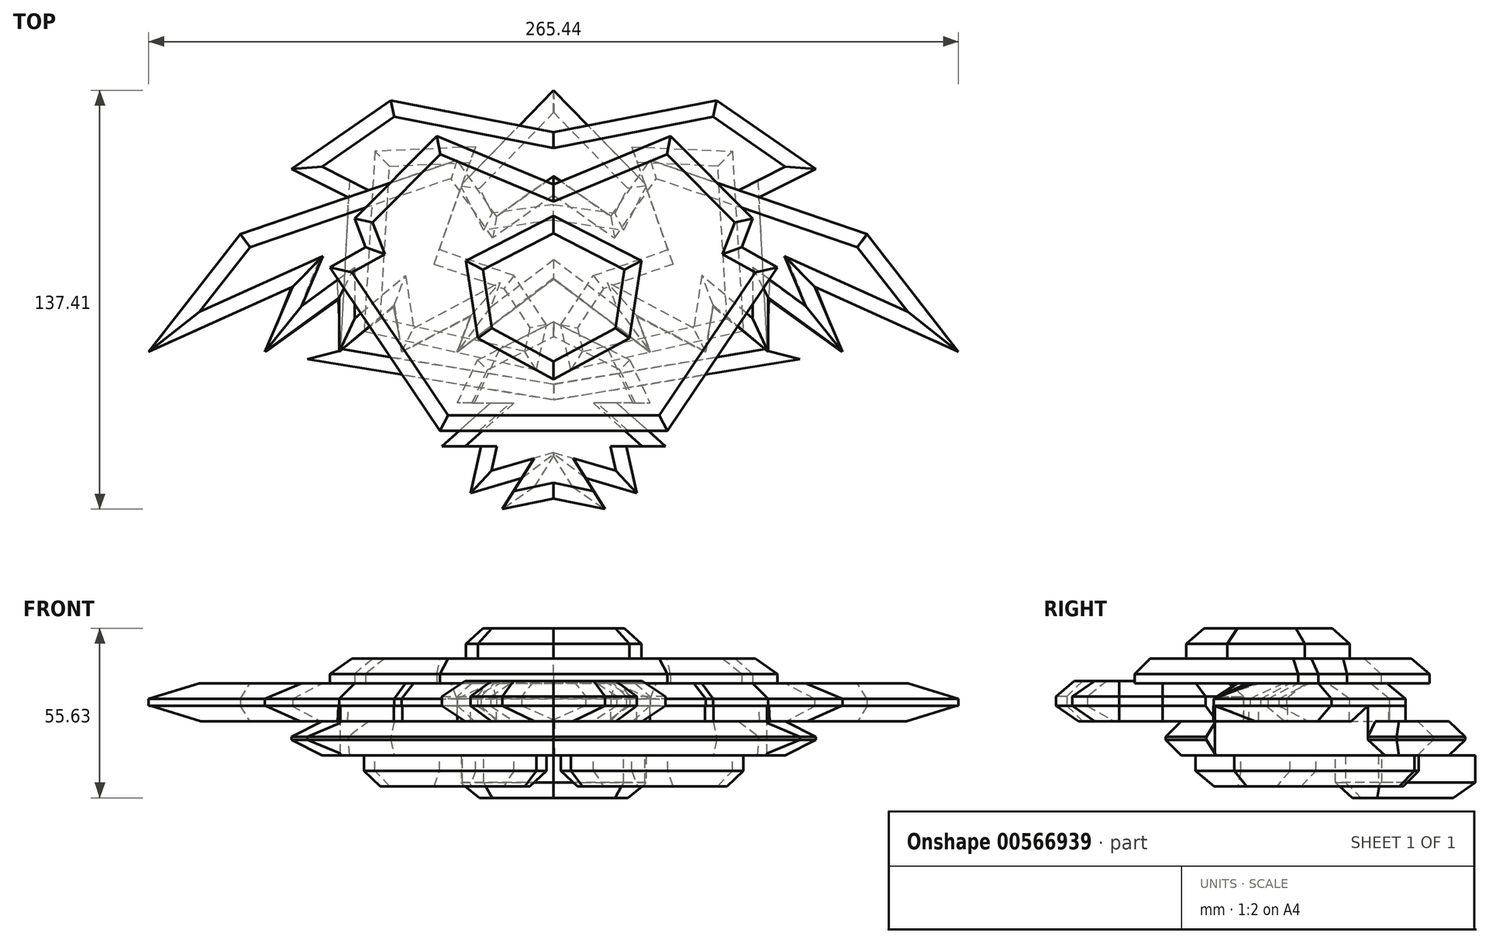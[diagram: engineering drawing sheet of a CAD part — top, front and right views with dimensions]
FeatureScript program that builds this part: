
annotation { "Feature Type Name" : "Feature", "Feature Type Description" : "" }
export const myFeature = defineFeature(function(context is Context, id is Id, definition is map)
    precondition{}
    {
        {
            var Q0;
            Q0=qCreatedBy(makeId("Top.planeOp"),FACE);
            var sketch = newSketch(context, id + "F0", { "sketchPlane" : qUnion([Q0])});
            skLineSegment(sketch, "E0", {"start": v(0, 55.5) * mm, "end": v(-18.73, 42.35) * mm});
            skLineSegment(sketch, "E1", {"start": v(-18.73, 42.35) * mm, "end": v(-31.67, 60.77) * mm});
            skLineSegment(sketch, "E2", {"start": v(-31.67, 60.77) * mm, "end": v(-102.63, 36.57) * mm});
            skLineSegment(sketch, "E3", {"start": v(-102.63, 36.57) * mm, "end": v(-132.72, -2.1) * mm});
            skLineSegment(sketch, "E4", {"start": v(-132.72, -2.1) * mm, "end": v(-85.5, 19.23) * mm});
            skLineSegment(sketch, "E5", {"start": v(-85.5, 19.23) * mm, "end": v(-94.66, -2.1) * mm});
            skLineSegment(sketch, "E6", {"start": v(-94.66, -2.1) * mm, "end": v(-70.35, 15.64) * mm});
            skLineSegment(sketch, "E7", {"start": v(-70.35, 15.64) * mm, "end": v(-70.35, -2.1) * mm});
            skLineSegment(sketch, "E8", {"start": v(-70.35, -2.1) * mm, "end": v(-52.21, 13.25) * mm});
            skLineSegment(sketch, "E9", {"start": v(-52.21, 13.25) * mm, "end": v(-49.82, -2.1) * mm});
            skLineSegment(sketch, "E10", {"start": v(-49.82, -2.1) * mm, "end": v(-27.1, 9.86) * mm});
            skLineSegment(sketch, "E11", {"start": v(-27.1, 9.86) * mm, "end": v(-31.67, -2.1) * mm});
            skLineSegment(sketch, "E12", {"start": v(-31.67, -2.1) * mm, "end": v(0, 21.82) * mm});
            skLineSegment(sketch, "E13", {"start": v(0, 21.82) * mm, "end": v(0, 55.5) * mm});
            skSolve(sketch);
        }
        {
            var Q0;
            Q0=makeQuery(id+"F0.imprint","IMPRINT",FACE,{"disambiguationData":[TD([[makeQuery(id+"F0.imprint","IMPRINT",EDGE,{"derivedFrom":sQuery(id+"F0.wireOp",EDGE,"E0")}),1.0]])]});
            extrude(context, id + "F1", {"entities" : qUnion([Q0]), "depth" : 7.37 * mm, "offsetDistance" : 25.4 * mm});
        }
        {
            var Q0;
            Q0=makeQuery(id+"F1.opExtrude","CAP_EDGE",EDGE,{"disambiguationData":[OSD([sQuery(id+"F0.wireOp",EDGE,"E2")])],"isStart":false});
            var Q1;
            Q1=makeQuery(id+"F1.opExtrude","CAP_EDGE",EDGE,{"disambiguationData":[OSD([sQuery(id+"F0.wireOp",EDGE,"E1")])],"isStart":false});
            var Q2;
            Q2=makeQuery(id+"F1.opExtrude","CAP_EDGE",EDGE,{"disambiguationData":[OSD([sQuery(id+"F0.wireOp",EDGE,"E0")])],"isStart":false});
            var Q3;
            Q3=makeQuery(id+"F1.opExtrude","CAP_EDGE",EDGE,{"disambiguationData":[OSD([sQuery(id+"F0.wireOp",EDGE,"E3")])],"isStart":false});
            var Q4;
            Q4=makeQuery(id+"F1.opExtrude","CAP_EDGE",EDGE,{"disambiguationData":[OSD([sQuery(id+"F0.wireOp",EDGE,"E4")])],"isStart":false});
            var Q5;
            Q5=makeQuery(id+"F1.opExtrude","CAP_EDGE",EDGE,{"disambiguationData":[OSD([sQuery(id+"F0.wireOp",EDGE,"E5")])],"isStart":false});
            var Q6;
            Q6=makeQuery(id+"F1.opExtrude","CAP_EDGE",EDGE,{"disambiguationData":[OSD([sQuery(id+"F0.wireOp",EDGE,"E6")])],"isStart":false});
            var Q7;
            Q7=makeQuery(id+"F1.opExtrude","CAP_EDGE",EDGE,{"disambiguationData":[OSD([sQuery(id+"F0.wireOp",EDGE,"E7")])],"isStart":false});
            var Q8;
            Q8=makeQuery(id+"F1.opExtrude","CAP_EDGE",EDGE,{"disambiguationData":[OSD([sQuery(id+"F0.wireOp",EDGE,"E8")])],"isStart":false});
            var Q9;
            Q9=makeQuery(id+"F1.opExtrude","CAP_EDGE",EDGE,{"disambiguationData":[OSD([sQuery(id+"F0.wireOp",EDGE,"E9")])],"isStart":false});
            var Q10;
            Q10=makeQuery(id+"F1.opExtrude","CAP_EDGE",EDGE,{"disambiguationData":[OSD([sQuery(id+"F0.wireOp",EDGE,"E10")])],"isStart":false});
            var Q11;
            Q11=makeQuery(id+"F1.opExtrude","CAP_EDGE",EDGE,{"disambiguationData":[OSD([sQuery(id+"F0.wireOp",EDGE,"E11")])],"isStart":false});
            var Q12;
            Q12=makeQuery(id+"F1.opExtrude","CAP_EDGE",EDGE,{"disambiguationData":[OSD([sQuery(id+"F0.wireOp",EDGE,"E12")])],"isStart":false});
            chamfer(context, id + "F2", {"entities" : qUnion([Q0, Q1, Q2, Q3, Q4, Q5, Q6, Q7, Q8, Q9, Q10, Q11, Q12]), "width" : 5.08 * mm, "tangentPropagation" : true});
        }
        {
            var Q0;
            Q0=makeQuery(id+"F1.opExtrude","CAP_FACE",FACE,{"disambiguationData":[OSD([sQuery(id+"F0.wireOp",EDGE,"E0"),sQuery(id+"F0.wireOp",EDGE,"E1"),sQuery(id+"F0.wireOp",EDGE,"E2"),sQuery(id+"F0.wireOp",EDGE,"E3"),sQuery(id+"F0.wireOp",EDGE,"E4"),sQuery(id+"F0.wireOp",EDGE,"E5"),sQuery(id+"F0.wireOp",EDGE,"E6"),sQuery(id+"F0.wireOp",EDGE,"E7"),sQuery(id+"F0.wireOp",EDGE,"E8"),sQuery(id+"F0.wireOp",EDGE,"E9"),sQuery(id+"F0.wireOp",EDGE,"E10"),sQuery(id+"F0.wireOp",EDGE,"E11"),sQuery(id+"F0.wireOp",EDGE,"E12"),sQuery(id+"F0.wireOp",EDGE,"E13")])],"isStart":true});
            var sketch = newSketch(context, id + "F3", { "sketchPlane" : qUnion([Q0])});
            skLineSegment(sketch, "E14", {"start": v(0.22, -55.6) * mm, "end": v(0.23, -22.25) * mm});
            skLineSegment(sketch, "E15", {"start": v(0.23, -22.25) * mm, "end": v(-31.54, 2.15) * mm});
            skLineSegment(sketch, "E16", {"start": v(-31.54, 2.15) * mm, "end": v(-27.3, -9.48) * mm});
            skLineSegment(sketch, "E17", {"start": v(-27.3, -9.48) * mm, "end": v(-49.58, 2.06) * mm});
            skLineSegment(sketch, "E18", {"start": v(-49.58, 2.06) * mm, "end": v(-52.4, -12.63) * mm});
            skLineSegment(sketch, "E19", {"start": v(-52.4, -12.63) * mm, "end": v(-69.93, 1.7) * mm});
            skLineSegment(sketch, "E20", {"start": v(-69.93, 1.7) * mm, "end": v(-70.6, -15.13) * mm});
            skLineSegment(sketch, "E21", {"start": v(-70.6, -15.13) * mm, "end": v(-94.41, 2.1) * mm});
            skLineSegment(sketch, "E22", {"start": v(-94.41, 2.1) * mm, "end": v(-85.86, -19.14) * mm});
            skLineSegment(sketch, "E23", {"start": v(-85.86, -19.14) * mm, "end": v(-132.03, 1.46) * mm});
            skLineSegment(sketch, "E24", {"start": v(-132.03, 1.46) * mm, "end": v(-102.76, -36.27) * mm});
            skLineSegment(sketch, "E25", {"start": v(-102.76, -36.27) * mm, "end": v(-31.67, -60.77) * mm});
            skLineSegment(sketch, "E26", {"start": v(-31.67, -60.77) * mm, "end": v(-18.73, -42.35) * mm});
            skLineSegment(sketch, "E27", {"start": v(-18.73, -42.35) * mm, "end": v(0.22, -55.6) * mm});
            skSolve(sketch);
        }
        {
            var Q0;
            Q0 = qSketchRegion(id + "F3", true);
            extrude(context, id + "F4", {"entities" : qUnion([Q0]), "operationType" : NewBodyOperationType.ADD, "depth" : 5.08 * mm, "offsetDistance" : 25.4 * mm});
        }
        {
            var Q0;
            Q0=makeQuery(id+"F4.opExtrude","CAP_FACE",FACE,{"disambiguationData":[OSD([sQuery(id+"F3.wireOp",EDGE,"E14"),sQuery(id+"F3.wireOp",EDGE,"E15"),sQuery(id+"F3.wireOp",EDGE,"E16"),sQuery(id+"F3.wireOp",EDGE,"E17"),sQuery(id+"F3.wireOp",EDGE,"E18"),sQuery(id+"F3.wireOp",EDGE,"E19"),sQuery(id+"F3.wireOp",EDGE,"E20"),sQuery(id+"F3.wireOp",EDGE,"E21"),sQuery(id+"F3.wireOp",EDGE,"E22"),sQuery(id+"F3.wireOp",EDGE,"E23"),sQuery(id+"F3.wireOp",EDGE,"E24"),sQuery(id+"F3.wireOp",EDGE,"E25"),sQuery(id+"F3.wireOp",EDGE,"E26"),sQuery(id+"F3.wireOp",EDGE,"E27")])],"isStart":false});
            var sketch = newSketch(context, id + "F5", { "sketchPlane" : qUnion([Q0])});
            skLineSegment(sketch, "E28", {"start": v(-67.22, -48.52) * mm, "end": v(-69.93, 1.7) * mm});
            skLineSegment(sketch, "E29", {"start": v(-69.93, 1.7) * mm, "end": v(-80.67, 4.48) * mm});
            skLineSegment(sketch, "E30", {"start": v(-80.67, 4.48) * mm, "end": v(0, 17.84) * mm});
            skLineSegment(sketch, "E31", {"start": v(0, 17.84) * mm, "end": v(0.22, -69.85) * mm});
            skPoint(sketch, "E31.endSnap0", {"position": v(0.22, -38.93) * mm});
            skLineSegment(sketch, "E32", {"start": v(0.22, -69.85) * mm, "end": v(-53.37, -80.4) * mm});
            skLineSegment(sketch, "E33", {"start": v(-53.37, -80.4) * mm, "end": v(-85.86, -57.9) * mm});
            skLineSegment(sketch, "E34", {"start": v(-85.86, -57.9) * mm, "end": v(-67.22, -48.52) * mm});
            skSolve(sketch);
        }
        {
            var Q0;
            Q0 = qSketchRegion(id + "F5", true);
            extrude(context, id + "F6", {"entities" : qUnion([Q0]), "operationType" : NewBodyOperationType.ADD, "depth" : 11.18 * mm, "offsetDistance" : 25.4 * mm});
        }
        {
            var Q0;
            Q0=makeQuery(id+"F6.opExtrude","CAP_EDGE",EDGE,{"disambiguationData":[OSD([sQuery(id+"F5.wireOp",EDGE,"E34")])],"isStart":false});
            var Q1;
            Q1=makeQuery(id+"F6.opExtrude","CAP_EDGE",EDGE,{"disambiguationData":[OSD([sQuery(id+"F5.wireOp",EDGE,"E33")])],"isStart":false});
            var Q2;
            Q2=makeQuery(id+"F6.opExtrude","CAP_EDGE",EDGE,{"disambiguationData":[OSD([sQuery(id+"F5.wireOp",EDGE,"E32")])],"isStart":false});
            var Q3;
            Q3=makeQuery(id+"F6.opExtrude","CAP_EDGE",EDGE,{"disambiguationData":[OSD([sQuery(id+"F5.wireOp",EDGE,"E30")])],"isStart":false});
            var Q4;
            Q4=makeQuery(id+"F6.opExtrude","CAP_EDGE",EDGE,{"disambiguationData":[OSD([sQuery(id+"F5.wireOp",EDGE,"E28")])],"isStart":true});
            chamfer(context, id + "F7", {"entities" : qUnion([Q0, Q1, Q2, Q3, Q4]), "width" : 5.08 * mm, "tangentPropagation" : true});
        }
        {
            var Q0;
            Q0=makeQuery(id+"F6.opExtrude","CAP_EDGE",EDGE,{"disambiguationData":[OSD([sQuery(id+"F5.wireOp",EDGE,"E33")])],"isStart":true});
            var Q1;
            Q1=makeQuery(id+"F6.opExtrude","CAP_EDGE",EDGE,{"disambiguationData":[OSD([sQuery(id+"F5.wireOp",EDGE,"E34")])],"isStart":true});
            var Q2;
            Q2=makeQuery(id+"F6.opExtrude","CAP_EDGE",EDGE,{"disambiguationData":[OSD([sQuery(id+"F5.wireOp",EDGE,"E32")])],"isStart":true});
            var Q3;
            Q3=makeQuery(id+"F6.opExtrude","CAP_EDGE",EDGE,{"disambiguationData":[OSD([sQuery(id+"F5.wireOp",EDGE,"E30")])],"isStart":true});
            chamfer(context, id + "F8", {"entities" : qUnion([Q0, Q1, Q2, Q3]), "width" : 5.08 * mm, "tangentPropagation" : true});
        }
        {
            var Q0;
            {var subQ0=sQuery(id+"F5.wireOp",EDGE,"E30");var subQ1=sQuery(id+"F5.wireOp",EDGE,"E29");var subQ7=sQuery(id+"F3.wireOp",EDGE,"E15");var subQ8=sQuery(id+"F5.wireOp",EDGE,"E28");var subQ9=sQuery(id+"F5.wireOp",EDGE,"E31");Q0=makeQuery(id+"F6.boolean.opBoolean","SPLIT",FACE,{"disambiguationData":[TD([makeQuery(id+"F4.opExtrude","SWEPT_FACE",FACE,{"disambiguationData":[OSD([subQ7])]})])],"derivedFrom":makeQuery(id+"F6.opExtrude","CAP_FACE",FACE,{"disambiguationData":[OSD([subQ8,subQ1,subQ0,subQ9,sQuery(id+"F5.wireOp",EDGE,"E32"),sQuery(id+"F5.wireOp",EDGE,"E33"),sQuery(id+"F5.wireOp",EDGE,"E34")])],"isStart":true})});}
            var sketch = newSketch(context, id + "F9", { "sketchPlane" : qUnion([Q0])});
            skLineSegment(sketch, "E35", {"start": v(-24.98, -4.76) * mm, "end": v(-31.54, -18.89) * mm});
            skLineSegment(sketch, "E36", {"start": v(-31.54, -18.89) * mm, "end": v(-20.68, -18.89) * mm});
            skLineSegment(sketch, "E37", {"start": v(-20.68, -18.89) * mm, "end": v(-36.66, -33.02) * mm});
            skLineSegment(sketch, "E38", {"start": v(-36.66, -33.02) * mm, "end": v(-23.75, -33.02) * mm});
            skLineSegment(sketch, "E39", {"start": v(-23.75, -33.02) * mm, "end": v(-27.24, -48.37) * mm});
            skLineSegment(sketch, "E40", {"start": v(-27.24, -48.37) * mm, "end": v(-10.44, -43.46) * mm});
            skLineSegment(sketch, "E41", {"start": v(-10.44, -43.46) * mm, "end": v(-16.8, -53.7) * mm});
            skLineSegment(sketch, "E42", {"start": v(-16.8, -53.7) * mm, "end": v(0.1, -50.22) * mm});
            skLineSegment(sketch, "E43", {"start": v(0.1, -50.22) * mm, "end": v(0.06, 7.74) * mm});
            skLineSegment(sketch, "E44", {"start": v(0.06, 7.74) * mm, "end": v(-24.98, -4.76) * mm});
            skSolve(sketch);
        }
        {
            var Q0;
            Q0 = qSketchRegion(id + "F9", true);
            extrude(context, id + "F10", {"entities" : qUnion([Q0]), "operationType" : NewBodyOperationType.ADD, "depth" : 13.2 * mm, "offsetDistance" : 25.4 * mm});
        }
        {
            var Q0;
            Q0=makeQuery(id+"F10.opExtrude","CAP_EDGE",EDGE,{"disambiguationData":[OSD([sQuery(id+"F9.wireOp",EDGE,"E44")])],"isStart":false});
            var Q1;
            Q1=makeQuery(id+"F10.opExtrude","CAP_EDGE",EDGE,{"disambiguationData":[OSD([sQuery(id+"F9.wireOp",EDGE,"E35")])],"isStart":false});
            var Q2;
            Q2=makeQuery(id+"F10.opExtrude","CAP_EDGE",EDGE,{"disambiguationData":[OSD([sQuery(id+"F9.wireOp",EDGE,"E37")])],"isStart":false});
            var Q3;
            Q3=makeQuery(id+"F10.opExtrude","CAP_EDGE",EDGE,{"disambiguationData":[OSD([sQuery(id+"F9.wireOp",EDGE,"E39")])],"isStart":false});
            var Q4;
            Q4=makeQuery(id+"F10.opExtrude","CAP_EDGE",EDGE,{"disambiguationData":[OSD([sQuery(id+"F9.wireOp",EDGE,"E40")])],"isStart":false});
            var Q5;
            Q5=makeQuery(id+"F10.opExtrude","CAP_EDGE",EDGE,{"disambiguationData":[OSD([sQuery(id+"F9.wireOp",EDGE,"E42")])],"isStart":false});
            var Q6;
            Q6=makeQuery(id+"F10.opExtrude","CAP_EDGE",EDGE,{"disambiguationData":[OSD([sQuery(id+"F9.wireOp",EDGE,"E41")])],"isStart":true});
            var Q7;
            Q7=makeQuery(id+"F10.opExtrude","CAP_EDGE",EDGE,{"disambiguationData":[OSD([sQuery(id+"F9.wireOp",EDGE,"E42")])],"isStart":true});
            var Q8;
            Q8=makeQuery(id+"F10.opExtrude","CAP_EDGE",EDGE,{"disambiguationData":[OSD([sQuery(id+"F9.wireOp",EDGE,"E40")])],"isStart":true});
            var Q9;
            Q9=makeQuery(id+"F10.opExtrude","CAP_EDGE",EDGE,{"disambiguationData":[OSD([sQuery(id+"F9.wireOp",EDGE,"E39")])],"isStart":true});
            var Q10;
            Q10=makeQuery(id+"F10.opExtrude","CAP_EDGE",EDGE,{"disambiguationData":[OSD([sQuery(id+"F9.wireOp",EDGE,"E37")])],"isStart":true});
            var Q11;
            {var subQ0=sQuery(id+"F9.wireOp",EDGE,"E35");Q11=makeQuery(id+"F10.boolean.opBoolean","SPLIT",EDGE,{"disambiguationData":[topologyDisambiguationEdgeConnected([makeQuery(id+"F10.opExtrude","CAP_FACE",FACE,{"disambiguationData":[OSD([subQ0,sQuery(id+"F9.wireOp",EDGE,"E36"),sQuery(id+"F9.wireOp",EDGE,"E37"),sQuery(id+"F9.wireOp",EDGE,"E38"),sQuery(id+"F9.wireOp",EDGE,"E39"),sQuery(id+"F9.wireOp",EDGE,"E40"),sQuery(id+"F9.wireOp",EDGE,"E41"),sQuery(id+"F9.wireOp",EDGE,"E42"),sQuery(id+"F9.wireOp",EDGE,"E43"),sQuery(id+"F9.wireOp",EDGE,"E44")])],"isStart":true})])],"derivedFrom":makeQuery(id+"F10.opExtrude","CAP_EDGE",EDGE,{"disambiguationData":[OSD([subQ0])],"isStart":true})});}
            chamfer(context, id + "F11", {"entities" : qUnion([Q0, Q1, Q2, Q3, Q4, Q5, Q6, Q7, Q8, Q9, Q10, Q11]), "width" : 5.08 * mm, "tangentPropagation" : true});
        }
        {
            var Q0;
            Q0=makeQuery(id+"F1.opExtrude","CAP_FACE",FACE,{"disambiguationData":[OSD([sQuery(id+"F0.wireOp",EDGE,"E0"),sQuery(id+"F0.wireOp",EDGE,"E1"),sQuery(id+"F0.wireOp",EDGE,"E2"),sQuery(id+"F0.wireOp",EDGE,"E3"),sQuery(id+"F0.wireOp",EDGE,"E4"),sQuery(id+"F0.wireOp",EDGE,"E5"),sQuery(id+"F0.wireOp",EDGE,"E6"),sQuery(id+"F0.wireOp",EDGE,"E7"),sQuery(id+"F0.wireOp",EDGE,"E8"),sQuery(id+"F0.wireOp",EDGE,"E9"),sQuery(id+"F0.wireOp",EDGE,"E10"),sQuery(id+"F0.wireOp",EDGE,"E11"),sQuery(id+"F0.wireOp",EDGE,"E12"),sQuery(id+"F0.wireOp",EDGE,"E13")])],"isStart":false});
            var sketch = newSketch(context, id + "F12", { "sketchPlane" : qUnion([Q0])});
            skLineSegment(sketch, "E45", {"start": v(0, 52.74) * mm, "end": v(-38.35, 68.67) * mm});
            skLineSegment(sketch, "E46", {"start": v(-38.35, 68.67) * mm, "end": v(-65.27, 41.6) * mm});
            skLineSegment(sketch, "E47", {"start": v(-65.27, 41.6) * mm, "end": v(-61.65, 32.25) * mm});
            skLineSegment(sketch, "E48", {"start": v(-61.65, 32.25) * mm, "end": v(-73.35, 25.64) * mm});
            skLineSegment(sketch, "E49", {"start": v(-73.35, 25.64) * mm, "end": v(-37.25, -28) * mm});
            skLineSegment(sketch, "E50", {"start": v(-37.25, -28) * mm, "end": v(0, -28) * mm});
            skLineSegment(sketch, "E51", {"start": v(0, -28) * mm, "end": v(0, 52.74) * mm});
            skSolve(sketch);
        }
        {
            var Q0;
            Q0 = qSketchRegion(id + "F12", true);
            extrude(context, id + "F13", {"entities" : qUnion([Q0]), "operationType" : NewBodyOperationType.ADD, "depth" : 8.13 * mm, "offsetDistance" : 25.4 * mm});
        }
        {
            var Q0;
            Q0=makeQuery(id+"F13.opExtrude","CAP_EDGE",EDGE,{"disambiguationData":[OSD([sQuery(id+"F12.wireOp",EDGE,"E46")])],"isStart":false});
            var Q1;
            Q1=makeQuery(id+"F13.opExtrude","CAP_EDGE",EDGE,{"disambiguationData":[OSD([sQuery(id+"F12.wireOp",EDGE,"E45")])],"isStart":false});
            var Q2;
            Q2=makeQuery(id+"F13.opExtrude","CAP_EDGE",EDGE,{"disambiguationData":[OSD([sQuery(id+"F12.wireOp",EDGE,"E48")])],"isStart":false});
            var Q3;
            Q3=makeQuery(id+"F13.opExtrude","CAP_EDGE",EDGE,{"disambiguationData":[OSD([sQuery(id+"F12.wireOp",EDGE,"E47")])],"isStart":false});
            var Q4;
            Q4=makeQuery(id+"F13.opExtrude","CAP_EDGE",EDGE,{"disambiguationData":[OSD([sQuery(id+"F12.wireOp",EDGE,"E49")])],"isStart":false});
            var Q5;
            Q5=makeQuery(id+"F13.opExtrude","CAP_EDGE",EDGE,{"disambiguationData":[OSD([sQuery(id+"F12.wireOp",EDGE,"E50")])],"isStart":false});
            chamfer(context, id + "F14", {"entities" : qUnion([Q0, Q1, Q2, Q3, Q4, Q5]), "width" : 5.08 * mm, "tangentPropagation" : true});
        }
        {
            var Q0;
            Q0=makeQuery(id+"F13.opExtrude","CAP_FACE",FACE,{"disambiguationData":[OSD([sQuery(id+"F12.wireOp",EDGE,"E45"),sQuery(id+"F12.wireOp",EDGE,"E46"),sQuery(id+"F12.wireOp",EDGE,"E47"),sQuery(id+"F12.wireOp",EDGE,"E48"),sQuery(id+"F12.wireOp",EDGE,"E49"),sQuery(id+"F12.wireOp",EDGE,"E50"),sQuery(id+"F12.wireOp",EDGE,"E51")])],"isStart":false});
            var sketch = newSketch(context, id + "F15", { "sketchPlane" : qUnion([Q0])});
            skLineSegment(sketch, "E52", {"start": v(0, 42.46) * mm, "end": v(-28.79, 27.72) * mm});
            skLineSegment(sketch, "E53", {"start": v(-28.79, 27.72) * mm, "end": v(-24.88, 2.39) * mm});
            skLineSegment(sketch, "E54", {"start": v(-24.88, 2.39) * mm, "end": v(0, -11.08) * mm});
            skLineSegment(sketch, "E55", {"start": v(0, -11.08) * mm, "end": v(0, 42.46) * mm});
            skSolve(sketch);
        }
        {
            var Q0;
            Q0=makeQuery(id+"F15.imprint","IMPRINT",FACE,{"disambiguationData":[TD([[makeQuery(id+"F15.imprint","IMPRINT",EDGE,{"derivedFrom":sQuery(id+"F15.wireOp",EDGE,"E52")}),1.0]])]});
            extrude(context, id + "F16", {"entities" : qUnion([Q0]), "operationType" : NewBodyOperationType.ADD, "depth" : 9.9 * mm, "offsetDistance" : 25.4 * mm});
        }
        {
            var Q0;
            Q0=makeQuery(id+"F16.opExtrude","CAP_EDGE",EDGE,{"disambiguationData":[OSD([sQuery(id+"F15.wireOp",EDGE,"E52")])],"isStart":false});
            var Q1;
            Q1=makeQuery(id+"F16.opExtrude","CAP_EDGE",EDGE,{"disambiguationData":[OSD([sQuery(id+"F15.wireOp",EDGE,"E53")])],"isStart":false});
            var Q2;
            Q2=makeQuery(id+"F16.opExtrude","CAP_EDGE",EDGE,{"disambiguationData":[OSD([sQuery(id+"F15.wireOp",EDGE,"E54")])],"isStart":false});
            chamfer(context, id + "F17", {"entities" : qUnion([Q0, Q1, Q2]), "width" : 5.08 * mm, "tangentPropagation" : true});
        }
        {
            var Q0;
            Q0=makeQuery(id+"F4.opExtrude","CAP_EDGE",EDGE,{"disambiguationData":[OSD([sQuery(id+"F3.wireOp",EDGE,"E21")])],"isStart":false});
            var Q1;
            Q1=makeQuery(id+"F4.opExtrude","CAP_EDGE",EDGE,{"disambiguationData":[OSD([sQuery(id+"F3.wireOp",EDGE,"E22")])],"isStart":false});
            var Q2;
            Q2=makeQuery(id+"F4.opExtrude","CAP_EDGE",EDGE,{"disambiguationData":[OSD([sQuery(id+"F3.wireOp",EDGE,"E23")])],"isStart":false});
            var Q3;
            Q3=makeQuery(id+"F4.opExtrude","CAP_EDGE",EDGE,{"disambiguationData":[OSD([sQuery(id+"F3.wireOp",EDGE,"E24")])],"isStart":false});
            var Q4;
            {var subQ0=sQuery(id+"F3.wireOp",EDGE,"E25");Q4=makeQuery(id+"F6.boolean.opBoolean","SPLIT",EDGE,{"disambiguationData":[topologyDisambiguationEdgeConnected([makeQuery(id+"F4.opExtrude","CAP_FACE",FACE,{"disambiguationData":[OSD([sQuery(id+"F3.wireOp",EDGE,"E14"),sQuery(id+"F3.wireOp",EDGE,"E15"),sQuery(id+"F3.wireOp",EDGE,"E16"),sQuery(id+"F3.wireOp",EDGE,"E17"),sQuery(id+"F3.wireOp",EDGE,"E18"),sQuery(id+"F3.wireOp",EDGE,"E19"),sQuery(id+"F3.wireOp",EDGE,"E20"),sQuery(id+"F3.wireOp",EDGE,"E21"),sQuery(id+"F3.wireOp",EDGE,"E22"),sQuery(id+"F3.wireOp",EDGE,"E23"),sQuery(id+"F3.wireOp",EDGE,"E24"),subQ0,sQuery(id+"F3.wireOp",EDGE,"E26"),sQuery(id+"F3.wireOp",EDGE,"E27")])],"isStart":false})])],"derivedFrom":makeQuery(id+"F4.opExtrude","CAP_EDGE",EDGE,{"disambiguationData":[OSD([subQ0])],"isStart":false})});}
            chamfer(context, id + "F18", {"entities" : qUnion([Q0, Q1, Q2, Q3, Q4]), "width" : 5.08 * mm, "tangentPropagation" : true});
        }
        {
            var Q0;
            Q0=makeQuery(id+"F6.opExtrude","CAP_FACE",FACE,{"disambiguationData":[OSD([sQuery(id+"F5.wireOp",EDGE,"E28"),sQuery(id+"F5.wireOp",EDGE,"E29"),sQuery(id+"F5.wireOp",EDGE,"E30"),sQuery(id+"F5.wireOp",EDGE,"E31"),sQuery(id+"F5.wireOp",EDGE,"E32"),sQuery(id+"F5.wireOp",EDGE,"E33"),sQuery(id+"F5.wireOp",EDGE,"E34")])],"isStart":false});
            var sketch = newSketch(context, id + "F19", { "sketchPlane" : qUnion([Q0])});
            skLineSegment(sketch, "E56", {"start": v(0.15, -41.11) * mm, "end": v(-22.94, -37.84) * mm});
            skLineSegment(sketch, "E57", {"start": v(-22.94, -37.84) * mm, "end": v(-30.51, -52.38) * mm});
            skLineSegment(sketch, "E58", {"start": v(-30.51, -52.38) * mm, "end": v(0, -83.7) * mm});
            skLineSegment(sketch, "E59", {"start": v(0, -83.7) * mm, "end": v(0.15, -41.11) * mm});
            skSolve(sketch);
        }
        {
            var Q0;
            {var subQ7=sQuery(id+"F19.wireOp",EDGE,"E56");Q0=makeQuery(id+"F19.imprint","IMPRINT",FACE,{"disambiguationData":[TD([[makeQuery(id+"F19.imprint","IMPRINT",EDGE,{"derivedFrom":subQ7}),1.0]])]});}
            var Q1;
            {var subQ0=sQuery(id+"F19.wireOp",EDGE,"E59");var subQ1=sQuery(id+"F19.wireOp",EDGE,"E58");var subQ2=makeQuery(id+"F19.imprint","INTERSECT",VERTEX,{"derivedFrom":[subQ1,subQ0]});Q1=makeQuery(id+"F19.imprint","IMPRINT",FACE,{"disambiguationData":[TD([[makeQuery(id+"F19.imprint","IMPRINT",EDGE,{"disambiguationData":[TD([[subQ2,1.0]])],"derivedFrom":subQ1}),1.0]])]});}
            extrude(context, id + "F20", {"entities" : qUnion([Q0, Q1]), "operationType" : NewBodyOperationType.ADD, "depth" : 13.97 * mm, "offsetDistance" : 25.4 * mm});
        }
        {
            var Q0;
            Q0=makeQuery(id+"F20.opExtrude","CAP_EDGE",EDGE,{"disambiguationData":[OSD([sQuery(id+"F19.wireOp",EDGE,"E56")])],"isStart":false});
            var Q1;
            Q1=makeQuery(id+"F20.opExtrude","CAP_EDGE",EDGE,{"disambiguationData":[OSD([sQuery(id+"F19.wireOp",EDGE,"E57")])],"isStart":false});
            var Q2;
            Q2=makeQuery(id+"F20.opExtrude","CAP_EDGE",EDGE,{"disambiguationData":[OSD([sQuery(id+"F19.wireOp",EDGE,"E58")])],"isStart":false});
            chamfer(context, id + "F21", {"entities" : qUnion([Q0, Q1, Q2]), "width" : 5.08 * mm, "tangentPropagation" : true});
        }
        {
            var Q0;
            {var subQ0=sQuery(id+"F19.wireOp",EDGE,"E57");var subQ1=sQuery(id+"F19.wireOp",EDGE,"E59");var subQ2=sQuery(id+"F19.wireOp",EDGE,"E58");var subQ3=sQuery(id+"F19.wireOp",EDGE,"E56");var subQ4=sQuery(id+"F5.wireOp",EDGE,"E33");var subQ5=sQuery(id+"F5.wireOp",EDGE,"E32");var subQ6=sQuery(id+"F5.wireOp",EDGE,"E34");var subQ7=sQuery(id+"F5.wireOp",EDGE,"E28");var subQ8=sQuery(id+"F5.wireOp",EDGE,"E31");var subQ9=sQuery(id+"F5.wireOp",EDGE,"E30");var subQ10=makeQuery(id+"F6.opExtrude","CAP_FACE",FACE,{"disambiguationData":[OSD([subQ7,sQuery(id+"F5.wireOp",EDGE,"E29"),subQ9,subQ8,subQ5,subQ4,subQ6])],"isStart":false});Q0=makeQuery(id+"F20.boolean.opBoolean","SPLIT",FACE,{"disambiguationData":[TD([makeQuery(id+"F6.opExtrude","SWEPT_FACE",FACE,{"disambiguationData":[OSD([subQ7])]}),subQ10,makeQuery(id+"F6.opExtrude","SWEPT_FACE",FACE,{"disambiguationData":[OSD([subQ8])]}),makeQuery(id+"F7.opChamfer","BLEND_FACE",FACE,{"disambiguationData":[OSD([subQ9])]}),makeQuery(id+"F7.opChamfer","BLEND_FACE",FACE,{"disambiguationData":[OSD([subQ5])]}),makeQuery(id+"F7.opChamfer","BLEND_FACE",FACE,{"disambiguationData":[OSD([subQ4])]}),makeQuery(id+"F7.opChamfer","BLEND_FACE",FACE,{"disambiguationData":[OSD([subQ6])]}),makeQuery(id+"F20.opExtrude","SWEPT_FACE",FACE,{"disambiguationData":[OSD([subQ3])]}),makeQuery(id+"F20.opExtrude","CAP_FACE",FACE,{"disambiguationData":[OSD([subQ3,subQ0,subQ2,subQ1])],"isStart":true}),makeQuery(id+"F20.opExtrude","SWEPT_FACE",FACE,{"disambiguationData":[OSD([subQ0])]}),makeQuery(id+"F20.opExtrude","SWEPT_FACE",FACE,{"disambiguationData":[OSD([subQ2])]}),makeQuery(id+"F20.opExtrude","SWEPT_FACE",FACE,{"disambiguationData":[OSD([subQ1])]})])],"derivedFrom":subQ10});}
            var sketch = newSketch(context, id + "F22", { "sketchPlane" : qUnion([Q0])});
            skLineSegment(sketch, "E60", {"start": v(-58.58, -63.66) * mm, "end": v(-62.13, -4.7) * mm});
            skLineSegment(sketch, "E61", {"start": v(-62.13, -4.7) * mm, "end": v(-5.68, 8.06) * mm});
            skLineSegment(sketch, "E62", {"start": v(-5.68, 8.06) * mm, "end": v(-2.32, -6.78) * mm});
            skLineSegment(sketch, "E63", {"start": v(-2.32, -6.78) * mm, "end": v(-13, -22.89) * mm});
            skLineSegment(sketch, "E64", {"start": v(-13, -22.89) * mm, "end": v(-37.46, -31.46) * mm});
            skLineSegment(sketch, "E65", {"start": v(-37.46, -31.46) * mm, "end": v(-25.65, -65.15) * mm});
            skLineSegment(sketch, "E66", {"start": v(-25.65, -65.15) * mm, "end": v(-58.58, -63.66) * mm});
            skSolve(sketch);
        }
        {
            var Q0;
            Q0 = qSketchRegion(id + "F22", true);
            extrude(context, id + "F23", {"entities" : qUnion([Q0]), "operationType" : NewBodyOperationType.ADD, "depth" : 10.16 * mm, "offsetDistance" : 25.4 * mm});
        }
        {
            var Q0;
            Q0=makeQuery(id+"F23.opExtrude","CAP_EDGE",EDGE,{"disambiguationData":[OSD([sQuery(id+"F22.wireOp",EDGE,"E61")])],"isStart":false});
            var Q1;
            Q1=makeQuery(id+"F23.opExtrude","CAP_EDGE",EDGE,{"disambiguationData":[OSD([sQuery(id+"F22.wireOp",EDGE,"E60")])],"isStart":false});
            var Q2;
            Q2=makeQuery(id+"F23.opExtrude","CAP_EDGE",EDGE,{"disambiguationData":[OSD([sQuery(id+"F22.wireOp",EDGE,"E66")])],"isStart":false});
            var Q3;
            Q3=makeQuery(id+"F23.opExtrude","CAP_EDGE",EDGE,{"disambiguationData":[OSD([sQuery(id+"F22.wireOp",EDGE,"E63")])],"isStart":false});
            var Q4;
            Q4=makeQuery(id+"F23.opExtrude","CAP_EDGE",EDGE,{"disambiguationData":[OSD([sQuery(id+"F22.wireOp",EDGE,"E62")])],"isStart":false});
            var Q5;
            Q5=makeQuery(id+"F23.opExtrude","CAP_EDGE",EDGE,{"disambiguationData":[OSD([sQuery(id+"F22.wireOp",EDGE,"E64")])],"isStart":true});
            var Q6;
            Q6=makeQuery(id+"F23.opExtrude","CAP_EDGE",EDGE,{"disambiguationData":[OSD([sQuery(id+"F22.wireOp",EDGE,"E64")])],"isStart":false});
            var Q7;
            Q7=makeQuery(id+"F23.opExtrude","CAP_EDGE",EDGE,{"disambiguationData":[OSD([sQuery(id+"F22.wireOp",EDGE,"E63")])],"isStart":true});
            var Q8;
            Q8=makeQuery(id+"F23.opExtrude","CAP_EDGE",EDGE,{"disambiguationData":[OSD([sQuery(id+"F22.wireOp",EDGE,"E60")])],"isStart":true});
            chamfer(context, id + "F24", {"entities" : qUnion([Q0, Q1, Q2, Q3, Q4, Q5, Q6, Q7, Q8]), "width" : 5.08 * mm, "tangentPropagation" : true});
        }
        {
            var Q0;
            Q0=makeQuery(id+"F1.opExtrude","SWEPT_BODY",BODY,{"disambiguationData":[OSD([sQuery(id+"F0.wireOp",EDGE,"E0"),sQuery(id+"F0.wireOp",EDGE,"E1"),sQuery(id+"F0.wireOp",EDGE,"E2"),sQuery(id+"F0.wireOp",EDGE,"E3"),sQuery(id+"F0.wireOp",EDGE,"E4"),sQuery(id+"F0.wireOp",EDGE,"E5"),sQuery(id+"F0.wireOp",EDGE,"E6"),sQuery(id+"F0.wireOp",EDGE,"E7"),sQuery(id+"F0.wireOp",EDGE,"E8"),sQuery(id+"F0.wireOp",EDGE,"E9"),sQuery(id+"F0.wireOp",EDGE,"E10"),sQuery(id+"F0.wireOp",EDGE,"E11"),sQuery(id+"F0.wireOp",EDGE,"E12"),sQuery(id+"F0.wireOp",EDGE,"E13")])]});
            var Q1;
            Q1=qCreatedBy(makeId("Right.planeOp"),FACE);
            mirror(context, id + "F25", {"operationType" : NewBodyOperationType.ADD, "entities" : qUnion([Q0]), "mirrorPlane" : qUnion([Q1])});
        }
    });
